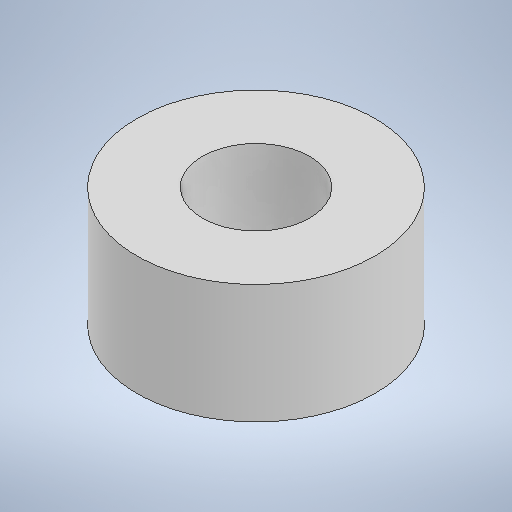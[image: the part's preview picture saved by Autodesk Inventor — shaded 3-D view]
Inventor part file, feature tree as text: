
AUTODESK INVENTOR PART (.ipt)
format: ipt  version: 2025.2 (Build 292293000, 293)  size: 196,096 bytes
history: native  units: mm
features: extrude x1, sketch x1
ambient origin geometry x8: Origin, YZ Plane, XZ Plane, XY Plane, X Axis, Y Axis, Z Axis, Center Point
bodies: Solid1 (feature_tree)
feature tree (2):
  extrude  "Extrusion1"  Depth=5.0mm
  sketch  "Sketch1"  dims[d0=10.0mm d1=4.5mm d2=5.0mm d3=0.0mm]
